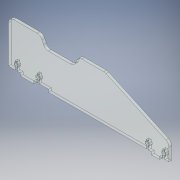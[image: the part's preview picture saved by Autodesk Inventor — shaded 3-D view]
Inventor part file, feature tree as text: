
AUTODESK INVENTOR PART (.ipt)
format: ipt  version: 2019 (Build 230136000, 136)  size: 281,088 bytes
history: native  units: mm
features: extrude x2, fillet x2, sketch x2
ambient origin geometry x8: Origin, YZ Plane, XZ Plane, XY Plane, X Axis, Y Axis, Z Axis, Center Point
bodies: Solid1 (feature_tree)
feature tree (6):
  extrude  "Extrusion1"  Depth=5.0mm TaperAngle=0.0deg
  fillet  "Fillet1"  Radius=10.0mm
  extrude  "Extrusion2"  Depth=10.0mm
  fillet  "Fillet2"  Radius=5.0mm
  sketch  "Sketch1"  dims[d0=127.0mm d1=110.5mm d2=80.0mm d3=75.0mm d4=189.5mm d5=85.0mm d6=55.0mm d7=40.0mm d8=5.0mm d9=17.5mm d10=30.0mm d11=5.0mm d12=42.5mm d13=37.0mm d14=15.0mm d15=5.0mm d16=0.0mm d17=10.0mm]
  sketch  "Sketch2"  dims[d18=50.0mm d19=30.0mm d20=127.0mm d21=110.5mm d22=80.0mm d23=75.0mm d24=189.5mm d25=85.0mm d26=55.0mm d27=25.0mm d28=5.0mm d29=27.5mm d30=15.0mm d31=5.0mm d32=67.0mm d33=5.0mm d34=30.0mm d35=30.0mm d36=17.5mm d37=6.0mm d38=4.0mm d39=15.0mm d40=8.0mm d41=4.0mm d42=4.0mm d43=8.0mm d44=6.0mm d45=4.0mm d46=15.0mm d47=6.0mm d48=4.0mm d49=15.0mm d50=6.0mm d51=8.0mm d52=4.0mm d53=8.0mm d54=7.0mm d55=7.0mm d56=12.5mm d57=5.0mm d58=0.0mm d59=30.0mm d60=10.0mm]
